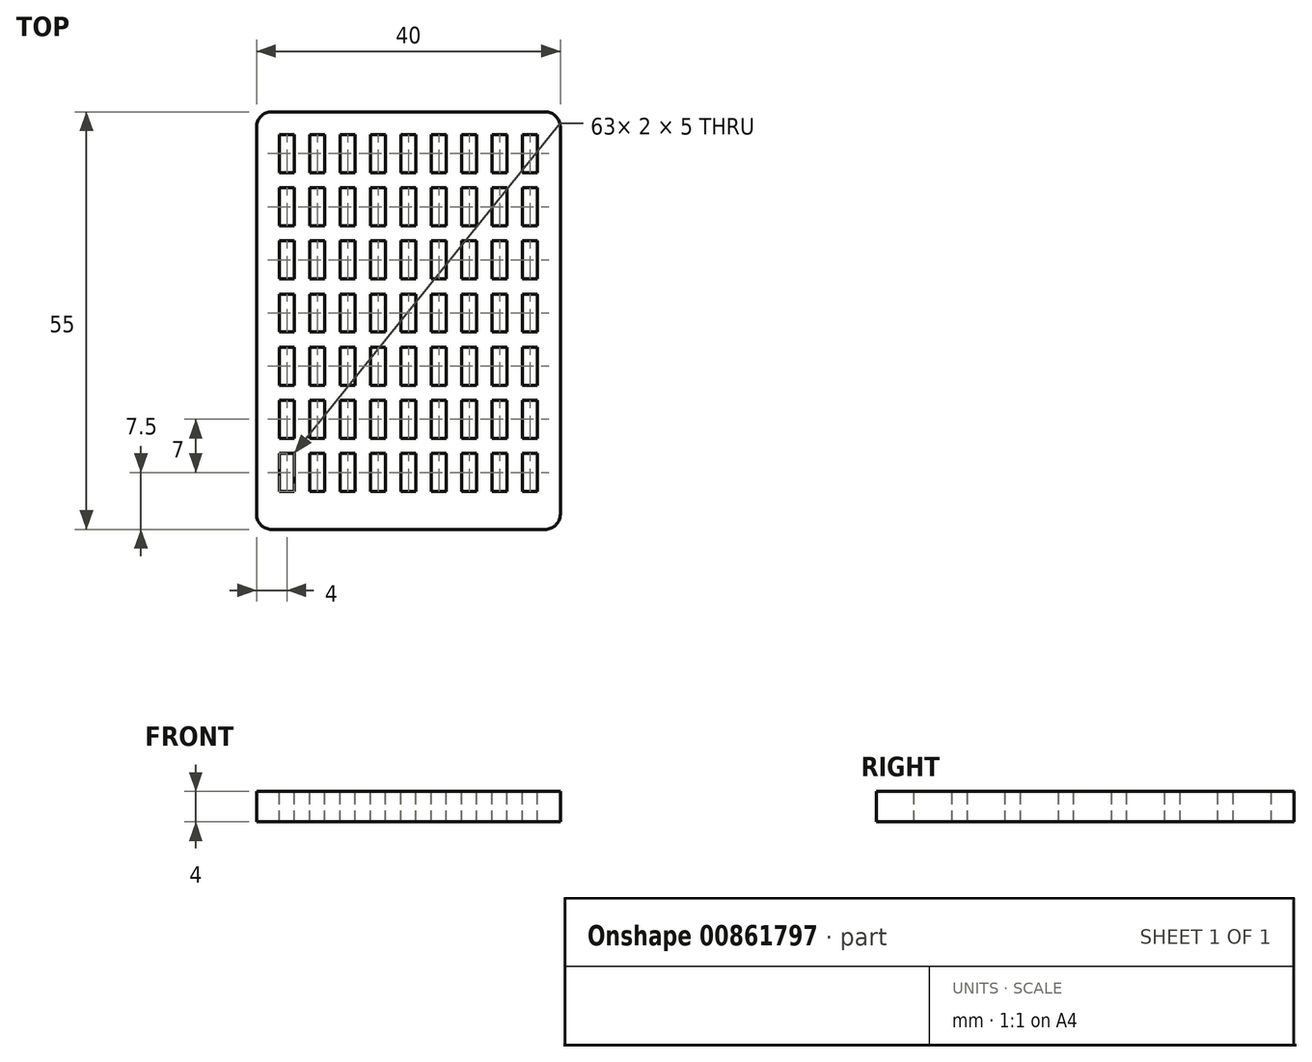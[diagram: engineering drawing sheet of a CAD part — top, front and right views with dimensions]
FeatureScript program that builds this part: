
annotation { "Feature Type Name" : "Feature", "Feature Type Description" : "" }
export const myFeature = defineFeature(function(context is Context, id is Id, definition is map)
    precondition{}
    {
        {
            var Q0;
            Q0=qCreatedBy(makeId("Top.planeOp"),FACE);
            var sketch = newSketch(context, id + "F0", { "sketchPlane" : qUnion([Q0])});
            skLineSegment(sketch, "E0.bottom", {"start": v(-20, 27.5) * mm, "end": v(20, 27.5) * mm});
            skLineSegment(sketch, "E0.top", {"start": v(-20, -27.5) * mm, "end": v(20, -27.5) * mm});
            skLineSegment(sketch, "E0.left", {"start": v(-20, 27.5) * mm, "end": v(-20, -27.5) * mm});
            skLineSegment(sketch, "E0.right", {"start": v(20, 27.5) * mm, "end": v(20, -27.5) * mm});
            skPoint(sketch, "E0.middle", {"position": v(0, 0) * mm});
            skSolve(sketch);
        }
        {
            var Q0;
            Q0 = qSketchRegion(id + "F0", true);
            extrude(context, id + "F1", {"entities" : qUnion([Q0]), "depth" : 4 * mm, "offsetDistance" : 25 * mm});
        }
        {
            var Q0;
            Q0=makeQuery(id+"F1.opExtrude","SWEPT_EDGE",EDGE,{"disambiguationData":[OSD([sQuery(id+"F0.wireOp",EDGE,"E0.bottom"),sQuery(id+"F0.wireOp",EDGE,"E0.left")])]});
            var Q1;
            Q1=makeQuery(id+"F1.opExtrude","SWEPT_EDGE",EDGE,{"disambiguationData":[OSD([sQuery(id+"F0.wireOp",EDGE,"E0.bottom"),sQuery(id+"F0.wireOp",EDGE,"E0.right")])]});
            var Q2;
            Q2=makeQuery(id+"F1.opExtrude","SWEPT_EDGE",EDGE,{"disambiguationData":[OSD([sQuery(id+"F0.wireOp",EDGE,"E0.top"),sQuery(id+"F0.wireOp",EDGE,"E0.left")])]});
            var Q3;
            Q3=makeQuery(id+"F1.opExtrude","SWEPT_EDGE",EDGE,{"disambiguationData":[OSD([sQuery(id+"F0.wireOp",EDGE,"E0.top"),sQuery(id+"F0.wireOp",EDGE,"E0.right")])]});
            fillet(context, id + "F2", {"entities" : qUnion([Q0, Q1, Q2, Q3]), "radius" : 2 * mm, "tangentPropagation" : true, "allowEdgeOverflow" : false});
        }
        {
            var Q0;
            Q0=makeQuery(id+"F1.opExtrude","CAP_FACE",FACE,{"disambiguationData":[OSD([sQuery(id+"F0.wireOp",EDGE,"E0.bottom"),sQuery(id+"F0.wireOp",EDGE,"E0.top"),sQuery(id+"F0.wireOp",EDGE,"E0.left"),sQuery(id+"F0.wireOp",EDGE,"E0.right")])],"isStart":false});
            var sketch = newSketch(context, id + "F3", { "sketchPlane" : qUnion([Q0])});
            skLineSegment(sketch, "E1.bottom", {"start": v(-17, 27.5) * mm, "end": v(-15, 27.5) * mm});
            skLineSegment(sketch, "E1.top", {"start": v(-17, -27.5) * mm, "end": v(-15, -27.5) * mm});
            skLineSegment(sketch, "E1.left", {"start": v(-17, 27.5) * mm, "end": v(-17, -27.5) * mm});
            skLineSegment(sketch, "E1.right", {"start": v(-15, 27.5) * mm, "end": v(-15, -27.5) * mm});
            skLineSegment(sketch, "E2.bottom", {"start": v(-13, -27.5) * mm, "end": v(-11, -27.5) * mm});
            skLineSegment(sketch, "E2.top", {"start": v(-13, 27.5) * mm, "end": v(-11, 27.5) * mm});
            skLineSegment(sketch, "E2.left", {"start": v(-13, -27.5) * mm, "end": v(-13, 27.5) * mm});
            skLineSegment(sketch, "E2.right", {"start": v(-11, -27.5) * mm, "end": v(-11, 27.5) * mm});
            skLineSegment(sketch, "E3.bottom", {"start": v(-9, 27.5) * mm, "end": v(-7, 27.5) * mm});
            skLineSegment(sketch, "E3.top", {"start": v(-9, -27.5) * mm, "end": v(-7, -27.5) * mm});
            skLineSegment(sketch, "E3.left", {"start": v(-9, 27.5) * mm, "end": v(-9, -27.5) * mm});
            skLineSegment(sketch, "E3.right", {"start": v(-7, 27.5) * mm, "end": v(-7, -27.5) * mm});
            skLineSegment(sketch, "E4.bottom", {"start": v(-5, -27.5) * mm, "end": v(-3, -27.5) * mm});
            skLineSegment(sketch, "E4.top", {"start": v(-5, 27.5) * mm, "end": v(-3, 27.5) * mm});
            skLineSegment(sketch, "E4.left", {"start": v(-5, -27.5) * mm, "end": v(-5, 27.5) * mm});
            skLineSegment(sketch, "E4.right", {"start": v(-3, -27.5) * mm, "end": v(-3, 27.5) * mm});
            skLineSegment(sketch, "E5.bottom", {"start": v(-1, 27.5) * mm, "end": v(1, 27.5) * mm});
            skLineSegment(sketch, "E5.top", {"start": v(-1, -27.5) * mm, "end": v(1, -27.5) * mm});
            skLineSegment(sketch, "E5.left", {"start": v(-1, 27.5) * mm, "end": v(-1, -27.5) * mm});
            skLineSegment(sketch, "E5.right", {"start": v(1, 27.5) * mm, "end": v(1, -27.5) * mm});
            skLineSegment(sketch, "E6.bottom", {"start": v(3, 27.5) * mm, "end": v(5, 27.5) * mm});
            skLineSegment(sketch, "E6.top", {"start": v(3, -27.5) * mm, "end": v(5, -27.5) * mm});
            skLineSegment(sketch, "E6.left", {"start": v(3, 27.5) * mm, "end": v(3, -27.5) * mm});
            skLineSegment(sketch, "E6.right", {"start": v(5, 27.5) * mm, "end": v(5, -27.5) * mm});
            skLineSegment(sketch, "E7.bottom", {"start": v(7, -27.5) * mm, "end": v(9, -27.5) * mm});
            skLineSegment(sketch, "E7.top", {"start": v(7, 27.5) * mm, "end": v(9, 27.5) * mm});
            skLineSegment(sketch, "E7.left", {"start": v(7, -27.5) * mm, "end": v(7, 27.5) * mm});
            skLineSegment(sketch, "E7.right", {"start": v(9, -27.5) * mm, "end": v(9, 27.5) * mm});
            skLineSegment(sketch, "E8.bottom", {"start": v(11, 27.5) * mm, "end": v(13, 27.5) * mm});
            skLineSegment(sketch, "E8.top", {"start": v(11, -27.5) * mm, "end": v(13, -27.5) * mm});
            skLineSegment(sketch, "E8.left", {"start": v(11, 27.5) * mm, "end": v(11, -27.5) * mm});
            skLineSegment(sketch, "E8.right", {"start": v(13, 27.5) * mm, "end": v(13, -27.5) * mm});
            skLineSegment(sketch, "E9.bottom", {"start": v(15, -27.5) * mm, "end": v(17, -27.5) * mm});
            skLineSegment(sketch, "E9.top", {"start": v(15, 27.5) * mm, "end": v(17, 27.5) * mm});
            skLineSegment(sketch, "E9.left", {"start": v(15, -27.5) * mm, "end": v(15, 27.5) * mm});
            skLineSegment(sketch, "E9.right", {"start": v(17, -27.5) * mm, "end": v(17, 27.5) * mm});
            skLineSegment(sketch, "E10.bottom", {"start": v(-20, 24.5) * mm, "end": v(20, 24.5) * mm});
            skLineSegment(sketch, "E10.top", {"start": v(-20, 19.5) * mm, "end": v(20, 19.5) * mm});
            skLineSegment(sketch, "E10.left", {"start": v(-20, 24.5) * mm, "end": v(-20, 19.5) * mm});
            skLineSegment(sketch, "E10.right", {"start": v(20, 24.5) * mm, "end": v(20, 19.5) * mm});
            skLineSegment(sketch, "E11.bottom", {"start": v(-20, 17.5) * mm, "end": v(20, 17.5) * mm});
            skLineSegment(sketch, "E11.top", {"start": v(-20, 12.5) * mm, "end": v(20, 12.5) * mm});
            skLineSegment(sketch, "E11.left", {"start": v(-20, 17.5) * mm, "end": v(-20, 12.5) * mm});
            skLineSegment(sketch, "E11.right", {"start": v(20, 17.5) * mm, "end": v(20, 12.5) * mm});
            skLineSegment(sketch, "E12.bottom", {"start": v(-20, 10.5) * mm, "end": v(20, 10.5) * mm});
            skLineSegment(sketch, "E12.top", {"start": v(-20, 5.5) * mm, "end": v(20, 5.5) * mm});
            skLineSegment(sketch, "E12.left", {"start": v(-20, 10.5) * mm, "end": v(-20, 5.5) * mm});
            skLineSegment(sketch, "E12.right", {"start": v(20, 10.5) * mm, "end": v(20, 5.5) * mm});
            skLineSegment(sketch, "E13.bottom", {"start": v(-20, 3.5) * mm, "end": v(20, 3.5) * mm});
            skLineSegment(sketch, "E13.top", {"start": v(-20, -1.5) * mm, "end": v(20, -1.5) * mm});
            skLineSegment(sketch, "E13.left", {"start": v(-20, 3.5) * mm, "end": v(-20, -1.5) * mm});
            skLineSegment(sketch, "E13.right", {"start": v(20, 3.5) * mm, "end": v(20, -1.5) * mm});
            skLineSegment(sketch, "E14.bottom", {"start": v(-20, -3.5) * mm, "end": v(20, -3.5) * mm});
            skLineSegment(sketch, "E14.top", {"start": v(-20, -8.5) * mm, "end": v(20, -8.5) * mm});
            skLineSegment(sketch, "E14.left", {"start": v(-20, -3.5) * mm, "end": v(-20, -8.5) * mm});
            skLineSegment(sketch, "E14.right", {"start": v(20, -3.5) * mm, "end": v(20, -8.5) * mm});
            skLineSegment(sketch, "E15.bottom", {"start": v(20, -8.5) * mm, "end": v(-20, -8.5) * mm});
            skLineSegment(sketch, "E15.top", {"start": v(20, -10.5) * mm, "end": v(-20, -10.5) * mm});
            skLineSegment(sketch, "E15.left", {"start": v(20, -8.5) * mm, "end": v(20, -10.5) * mm});
            skLineSegment(sketch, "E15.right", {"start": v(-20, -8.5) * mm, "end": v(-20, -10.5) * mm});
            skLineSegment(sketch, "E16.bottom", {"start": v(-20, -15.5) * mm, "end": v(20, -15.5) * mm});
            skLineSegment(sketch, "E16.top", {"start": v(-20, -17.5) * mm, "end": v(20, -17.5) * mm});
            skLineSegment(sketch, "E16.left", {"start": v(-20, -15.5) * mm, "end": v(-20, -17.5) * mm});
            skLineSegment(sketch, "E16.right", {"start": v(20, -15.5) * mm, "end": v(20, -17.5) * mm});
            skLineSegment(sketch, "E17.bottom", {"start": v(20, -22.5) * mm, "end": v(-20, -22.5) * mm});
            skLineSegment(sketch, "E17.top", {"start": v(20, -24.5) * mm, "end": v(-20, -24.5) * mm});
            skLineSegment(sketch, "E17.left", {"start": v(20, -22.5) * mm, "end": v(20, -24.5) * mm});
            skLineSegment(sketch, "E17.right", {"start": v(-20, -22.5) * mm, "end": v(-20, -24.5) * mm});
            skSolve(sketch);
        }
        {
            var Q0;
            {var subQ0=sQuery(id+"F3.wireOp",EDGE,"E10.bottom");var subQ1=sQuery(id+"F3.wireOp",EDGE,"E1.left");var subQ2=makeQuery(id+"F3.imprint","INTERSECT",VERTEX,{"derivedFrom":[subQ1,subQ0]});Q0=makeQuery(id+"F3.imprint","IMPRINT",FACE,{"disambiguationData":[TD([[makeQuery(id+"F3.imprint","IMPRINT",EDGE,{"disambiguationData":[TD([[subQ2,-1.0]])],"derivedFrom":subQ1}),1.0]])]});}
            var Q1;
            {var subQ0=sQuery(id+"F3.wireOp",EDGE,"E11.bottom");var subQ1=sQuery(id+"F3.wireOp",EDGE,"E1.left");var subQ2=makeQuery(id+"F3.imprint","INTERSECT",VERTEX,{"derivedFrom":[subQ1,subQ0]});Q1=makeQuery(id+"F3.imprint","IMPRINT",FACE,{"disambiguationData":[TD([[makeQuery(id+"F3.imprint","IMPRINT",EDGE,{"disambiguationData":[TD([[subQ2,-1.0]])],"derivedFrom":subQ1}),1.0]])]});}
            var Q2;
            {var subQ0=sQuery(id+"F3.wireOp",EDGE,"E12.bottom");var subQ1=sQuery(id+"F3.wireOp",EDGE,"E1.left");var subQ2=makeQuery(id+"F3.imprint","INTERSECT",VERTEX,{"derivedFrom":[subQ1,subQ0]});Q2=makeQuery(id+"F3.imprint","IMPRINT",FACE,{"disambiguationData":[TD([[makeQuery(id+"F3.imprint","IMPRINT",EDGE,{"disambiguationData":[TD([[subQ2,-1.0]])],"derivedFrom":subQ1}),1.0]])]});}
            var Q3;
            {var subQ0=sQuery(id+"F3.wireOp",EDGE,"E13.bottom");var subQ1=sQuery(id+"F3.wireOp",EDGE,"E1.left");var subQ2=makeQuery(id+"F3.imprint","INTERSECT",VERTEX,{"derivedFrom":[subQ1,subQ0]});Q3=makeQuery(id+"F3.imprint","IMPRINT",FACE,{"disambiguationData":[TD([[makeQuery(id+"F3.imprint","IMPRINT",EDGE,{"disambiguationData":[TD([[subQ2,-1.0]])],"derivedFrom":subQ1}),1.0]])]});}
            var Q4;
            {var subQ0=sQuery(id+"F3.wireOp",EDGE,"E14.bottom");var subQ1=sQuery(id+"F3.wireOp",EDGE,"E1.left");var subQ2=makeQuery(id+"F3.imprint","INTERSECT",VERTEX,{"derivedFrom":[subQ1,subQ0]});Q4=makeQuery(id+"F3.imprint","IMPRINT",FACE,{"disambiguationData":[TD([[makeQuery(id+"F3.imprint","IMPRINT",EDGE,{"disambiguationData":[TD([[subQ2,-1.0]])],"derivedFrom":subQ1}),1.0]])]});}
            var Q5;
            {var subQ0=sQuery(id+"F3.wireOp",EDGE,"E15.top");var subQ1=sQuery(id+"F3.wireOp",EDGE,"E1.left");var subQ2=makeQuery(id+"F3.imprint","INTERSECT",VERTEX,{"derivedFrom":[subQ1,subQ0]});Q5=makeQuery(id+"F3.imprint","IMPRINT",FACE,{"disambiguationData":[TD([[makeQuery(id+"F3.imprint","IMPRINT",EDGE,{"disambiguationData":[TD([[subQ2,-1.0]])],"derivedFrom":subQ1}),1.0]])]});}
            var Q6;
            {var subQ0=sQuery(id+"F3.wireOp",EDGE,"E17.bottom");var subQ1=sQuery(id+"F3.wireOp",EDGE,"E2.left");var subQ2=makeQuery(id+"F3.imprint","INTERSECT",VERTEX,{"derivedFrom":[subQ1,subQ0]});Q6=makeQuery(id+"F3.imprint","IMPRINT",FACE,{"disambiguationData":[TD([[makeQuery(id+"F3.imprint","IMPRINT",EDGE,{"disambiguationData":[TD([[subQ2,-1.0]])],"derivedFrom":subQ1}),-1.0]])]});}
            var Q7;
            {var subQ0=sQuery(id+"F3.wireOp",EDGE,"E16.bottom");var subQ1=sQuery(id+"F3.wireOp",EDGE,"E2.left");var subQ2=makeQuery(id+"F3.imprint","INTERSECT",VERTEX,{"derivedFrom":[subQ1,subQ0]});Q7=makeQuery(id+"F3.imprint","IMPRINT",FACE,{"disambiguationData":[TD([[makeQuery(id+"F3.imprint","IMPRINT",EDGE,{"disambiguationData":[TD([[subQ2,-1.0]])],"derivedFrom":subQ1}),-1.0]])]});}
            var Q8;
            {var subQ0=sQuery(id+"F3.wireOp",EDGE,"E15.bottom");var subQ1=sQuery(id+"F3.wireOp",EDGE,"E2.left");var subQ2=makeQuery(id+"F3.imprint","INTERSECT",VERTEX,{"derivedFrom":[subQ1,subQ0]});Q8=makeQuery(id+"F3.imprint","IMPRINT",FACE,{"disambiguationData":[TD([[makeQuery(id+"F3.imprint","IMPRINT",EDGE,{"disambiguationData":[TD([[subQ2,-1.0]])],"derivedFrom":subQ1}),-1.0]])]});}
            var Q9;
            {var subQ0=sQuery(id+"F3.wireOp",EDGE,"E13.top");var subQ1=sQuery(id+"F3.wireOp",EDGE,"E2.left");var subQ2=makeQuery(id+"F3.imprint","INTERSECT",VERTEX,{"derivedFrom":[subQ1,subQ0]});Q9=makeQuery(id+"F3.imprint","IMPRINT",FACE,{"disambiguationData":[TD([[makeQuery(id+"F3.imprint","IMPRINT",EDGE,{"disambiguationData":[TD([[subQ2,-1.0]])],"derivedFrom":subQ1}),-1.0]])]});}
            var Q10;
            {var subQ0=sQuery(id+"F3.wireOp",EDGE,"E12.top");var subQ1=sQuery(id+"F3.wireOp",EDGE,"E2.left");var subQ2=makeQuery(id+"F3.imprint","INTERSECT",VERTEX,{"derivedFrom":[subQ1,subQ0]});Q10=makeQuery(id+"F3.imprint","IMPRINT",FACE,{"disambiguationData":[TD([[makeQuery(id+"F3.imprint","IMPRINT",EDGE,{"disambiguationData":[TD([[subQ2,-1.0]])],"derivedFrom":subQ1}),-1.0]])]});}
            var Q11;
            {var subQ0=sQuery(id+"F3.wireOp",EDGE,"E11.top");var subQ1=sQuery(id+"F3.wireOp",EDGE,"E2.left");var subQ2=makeQuery(id+"F3.imprint","INTERSECT",VERTEX,{"derivedFrom":[subQ1,subQ0]});Q11=makeQuery(id+"F3.imprint","IMPRINT",FACE,{"disambiguationData":[TD([[makeQuery(id+"F3.imprint","IMPRINT",EDGE,{"disambiguationData":[TD([[subQ2,-1.0]])],"derivedFrom":subQ1}),-1.0]])]});}
            var Q12;
            {var subQ0=sQuery(id+"F3.wireOp",EDGE,"E10.top");var subQ1=sQuery(id+"F3.wireOp",EDGE,"E2.left");var subQ2=makeQuery(id+"F3.imprint","INTERSECT",VERTEX,{"derivedFrom":[subQ1,subQ0]});Q12=makeQuery(id+"F3.imprint","IMPRINT",FACE,{"disambiguationData":[TD([[makeQuery(id+"F3.imprint","IMPRINT",EDGE,{"disambiguationData":[TD([[subQ2,-1.0]])],"derivedFrom":subQ1}),-1.0]])]});}
            var Q13;
            {var subQ0=sQuery(id+"F3.wireOp",EDGE,"E10.bottom");var subQ1=sQuery(id+"F3.wireOp",EDGE,"E3.left");var subQ2=makeQuery(id+"F3.imprint","INTERSECT",VERTEX,{"derivedFrom":[subQ1,subQ0]});Q13=makeQuery(id+"F3.imprint","IMPRINT",FACE,{"disambiguationData":[TD([[makeQuery(id+"F3.imprint","IMPRINT",EDGE,{"disambiguationData":[TD([[subQ2,-1.0]])],"derivedFrom":subQ1}),1.0]])]});}
            var Q14;
            {var subQ0=sQuery(id+"F3.wireOp",EDGE,"E11.bottom");var subQ1=sQuery(id+"F3.wireOp",EDGE,"E3.left");var subQ2=makeQuery(id+"F3.imprint","INTERSECT",VERTEX,{"derivedFrom":[subQ1,subQ0]});Q14=makeQuery(id+"F3.imprint","IMPRINT",FACE,{"disambiguationData":[TD([[makeQuery(id+"F3.imprint","IMPRINT",EDGE,{"disambiguationData":[TD([[subQ2,-1.0]])],"derivedFrom":subQ1}),1.0]])]});}
            var Q15;
            {var subQ0=sQuery(id+"F3.wireOp",EDGE,"E12.bottom");var subQ1=sQuery(id+"F3.wireOp",EDGE,"E3.left");var subQ2=makeQuery(id+"F3.imprint","INTERSECT",VERTEX,{"derivedFrom":[subQ1,subQ0]});Q15=makeQuery(id+"F3.imprint","IMPRINT",FACE,{"disambiguationData":[TD([[makeQuery(id+"F3.imprint","IMPRINT",EDGE,{"disambiguationData":[TD([[subQ2,-1.0]])],"derivedFrom":subQ1}),1.0]])]});}
            var Q16;
            {var subQ0=sQuery(id+"F3.wireOp",EDGE,"E13.bottom");var subQ1=sQuery(id+"F3.wireOp",EDGE,"E3.left");var subQ2=makeQuery(id+"F3.imprint","INTERSECT",VERTEX,{"derivedFrom":[subQ1,subQ0]});Q16=makeQuery(id+"F3.imprint","IMPRINT",FACE,{"disambiguationData":[TD([[makeQuery(id+"F3.imprint","IMPRINT",EDGE,{"disambiguationData":[TD([[subQ2,-1.0]])],"derivedFrom":subQ1}),1.0]])]});}
            var Q17;
            {var subQ0=sQuery(id+"F3.wireOp",EDGE,"E14.bottom");var subQ1=sQuery(id+"F3.wireOp",EDGE,"E3.left");var subQ2=makeQuery(id+"F3.imprint","INTERSECT",VERTEX,{"derivedFrom":[subQ1,subQ0]});Q17=makeQuery(id+"F3.imprint","IMPRINT",FACE,{"disambiguationData":[TD([[makeQuery(id+"F3.imprint","IMPRINT",EDGE,{"disambiguationData":[TD([[subQ2,-1.0]])],"derivedFrom":subQ1}),1.0]])]});}
            var Q18;
            {var subQ0=sQuery(id+"F3.wireOp",EDGE,"E15.top");var subQ1=sQuery(id+"F3.wireOp",EDGE,"E3.left");var subQ2=makeQuery(id+"F3.imprint","INTERSECT",VERTEX,{"derivedFrom":[subQ1,subQ0]});Q18=makeQuery(id+"F3.imprint","IMPRINT",FACE,{"disambiguationData":[TD([[makeQuery(id+"F3.imprint","IMPRINT",EDGE,{"disambiguationData":[TD([[subQ2,-1.0]])],"derivedFrom":subQ1}),1.0]])]});}
            var Q19;
            {var subQ0=sQuery(id+"F3.wireOp",EDGE,"E16.top");var subQ1=sQuery(id+"F3.wireOp",EDGE,"E1.left");var subQ2=makeQuery(id+"F3.imprint","INTERSECT",VERTEX,{"derivedFrom":[subQ1,subQ0]});Q19=makeQuery(id+"F3.imprint","IMPRINT",FACE,{"disambiguationData":[TD([[makeQuery(id+"F3.imprint","IMPRINT",EDGE,{"disambiguationData":[TD([[subQ2,-1.0]])],"derivedFrom":subQ1}),1.0]])]});}
            var Q20;
            {var subQ0=sQuery(id+"F3.wireOp",EDGE,"E16.top");var subQ1=sQuery(id+"F3.wireOp",EDGE,"E3.left");var subQ2=makeQuery(id+"F3.imprint","INTERSECT",VERTEX,{"derivedFrom":[subQ1,subQ0]});Q20=makeQuery(id+"F3.imprint","IMPRINT",FACE,{"disambiguationData":[TD([[makeQuery(id+"F3.imprint","IMPRINT",EDGE,{"disambiguationData":[TD([[subQ2,-1.0]])],"derivedFrom":subQ1}),1.0]])]});}
            var Q21;
            {var subQ0=sQuery(id+"F3.wireOp",EDGE,"E17.bottom");var subQ1=sQuery(id+"F3.wireOp",EDGE,"E4.left");var subQ2=makeQuery(id+"F3.imprint","INTERSECT",VERTEX,{"derivedFrom":[subQ1,subQ0]});Q21=makeQuery(id+"F3.imprint","IMPRINT",FACE,{"disambiguationData":[TD([[makeQuery(id+"F3.imprint","IMPRINT",EDGE,{"disambiguationData":[TD([[subQ2,-1.0]])],"derivedFrom":subQ1}),-1.0]])]});}
            var Q22;
            {var subQ0=sQuery(id+"F3.wireOp",EDGE,"E16.bottom");var subQ1=sQuery(id+"F3.wireOp",EDGE,"E4.left");var subQ2=makeQuery(id+"F3.imprint","INTERSECT",VERTEX,{"derivedFrom":[subQ1,subQ0]});Q22=makeQuery(id+"F3.imprint","IMPRINT",FACE,{"disambiguationData":[TD([[makeQuery(id+"F3.imprint","IMPRINT",EDGE,{"disambiguationData":[TD([[subQ2,-1.0]])],"derivedFrom":subQ1}),-1.0]])]});}
            var Q23;
            {var subQ0=sQuery(id+"F3.wireOp",EDGE,"E15.bottom");var subQ1=sQuery(id+"F3.wireOp",EDGE,"E4.left");var subQ2=makeQuery(id+"F3.imprint","INTERSECT",VERTEX,{"derivedFrom":[subQ1,subQ0]});Q23=makeQuery(id+"F3.imprint","IMPRINT",FACE,{"disambiguationData":[TD([[makeQuery(id+"F3.imprint","IMPRINT",EDGE,{"disambiguationData":[TD([[subQ2,-1.0]])],"derivedFrom":subQ1}),-1.0]])]});}
            var Q24;
            {var subQ0=sQuery(id+"F3.wireOp",EDGE,"E13.top");var subQ1=sQuery(id+"F3.wireOp",EDGE,"E4.left");var subQ2=makeQuery(id+"F3.imprint","INTERSECT",VERTEX,{"derivedFrom":[subQ1,subQ0]});Q24=makeQuery(id+"F3.imprint","IMPRINT",FACE,{"disambiguationData":[TD([[makeQuery(id+"F3.imprint","IMPRINT",EDGE,{"disambiguationData":[TD([[subQ2,-1.0]])],"derivedFrom":subQ1}),-1.0]])]});}
            var Q25;
            {var subQ0=sQuery(id+"F3.wireOp",EDGE,"E12.top");var subQ1=sQuery(id+"F3.wireOp",EDGE,"E4.left");var subQ2=makeQuery(id+"F3.imprint","INTERSECT",VERTEX,{"derivedFrom":[subQ1,subQ0]});Q25=makeQuery(id+"F3.imprint","IMPRINT",FACE,{"disambiguationData":[TD([[makeQuery(id+"F3.imprint","IMPRINT",EDGE,{"disambiguationData":[TD([[subQ2,-1.0]])],"derivedFrom":subQ1}),-1.0]])]});}
            var Q26;
            {var subQ0=sQuery(id+"F3.wireOp",EDGE,"E11.top");var subQ1=sQuery(id+"F3.wireOp",EDGE,"E4.left");var subQ2=makeQuery(id+"F3.imprint","INTERSECT",VERTEX,{"derivedFrom":[subQ1,subQ0]});Q26=makeQuery(id+"F3.imprint","IMPRINT",FACE,{"disambiguationData":[TD([[makeQuery(id+"F3.imprint","IMPRINT",EDGE,{"disambiguationData":[TD([[subQ2,-1.0]])],"derivedFrom":subQ1}),-1.0]])]});}
            var Q27;
            {var subQ0=sQuery(id+"F3.wireOp",EDGE,"E10.top");var subQ1=sQuery(id+"F3.wireOp",EDGE,"E4.left");var subQ2=makeQuery(id+"F3.imprint","INTERSECT",VERTEX,{"derivedFrom":[subQ1,subQ0]});Q27=makeQuery(id+"F3.imprint","IMPRINT",FACE,{"disambiguationData":[TD([[makeQuery(id+"F3.imprint","IMPRINT",EDGE,{"disambiguationData":[TD([[subQ2,-1.0]])],"derivedFrom":subQ1}),-1.0]])]});}
            var Q28;
            {var subQ0=sQuery(id+"F3.wireOp",EDGE,"E10.bottom");var subQ1=sQuery(id+"F3.wireOp",EDGE,"E5.left");var subQ2=makeQuery(id+"F3.imprint","INTERSECT",VERTEX,{"derivedFrom":[subQ1,subQ0]});Q28=makeQuery(id+"F3.imprint","IMPRINT",FACE,{"disambiguationData":[TD([[makeQuery(id+"F3.imprint","IMPRINT",EDGE,{"disambiguationData":[TD([[subQ2,-1.0]])],"derivedFrom":subQ1}),1.0]])]});}
            var Q29;
            {var subQ0=sQuery(id+"F3.wireOp",EDGE,"E11.bottom");var subQ1=sQuery(id+"F3.wireOp",EDGE,"E5.left");var subQ2=makeQuery(id+"F3.imprint","INTERSECT",VERTEX,{"derivedFrom":[subQ1,subQ0]});Q29=makeQuery(id+"F3.imprint","IMPRINT",FACE,{"disambiguationData":[TD([[makeQuery(id+"F3.imprint","IMPRINT",EDGE,{"disambiguationData":[TD([[subQ2,-1.0]])],"derivedFrom":subQ1}),1.0]])]});}
            var Q30;
            {var subQ0=sQuery(id+"F3.wireOp",EDGE,"E12.bottom");var subQ1=sQuery(id+"F3.wireOp",EDGE,"E5.left");var subQ2=makeQuery(id+"F3.imprint","INTERSECT",VERTEX,{"derivedFrom":[subQ1,subQ0]});Q30=makeQuery(id+"F3.imprint","IMPRINT",FACE,{"disambiguationData":[TD([[makeQuery(id+"F3.imprint","IMPRINT",EDGE,{"disambiguationData":[TD([[subQ2,-1.0]])],"derivedFrom":subQ1}),1.0]])]});}
            var Q31;
            {var subQ0=sQuery(id+"F3.wireOp",EDGE,"E13.bottom");var subQ1=sQuery(id+"F3.wireOp",EDGE,"E5.left");var subQ2=makeQuery(id+"F3.imprint","INTERSECT",VERTEX,{"derivedFrom":[subQ1,subQ0]});Q31=makeQuery(id+"F3.imprint","IMPRINT",FACE,{"disambiguationData":[TD([[makeQuery(id+"F3.imprint","IMPRINT",EDGE,{"disambiguationData":[TD([[subQ2,-1.0]])],"derivedFrom":subQ1}),1.0]])]});}
            var Q32;
            {var subQ0=sQuery(id+"F3.wireOp",EDGE,"E14.bottom");var subQ1=sQuery(id+"F3.wireOp",EDGE,"E5.left");var subQ2=makeQuery(id+"F3.imprint","INTERSECT",VERTEX,{"derivedFrom":[subQ1,subQ0]});Q32=makeQuery(id+"F3.imprint","IMPRINT",FACE,{"disambiguationData":[TD([[makeQuery(id+"F3.imprint","IMPRINT",EDGE,{"disambiguationData":[TD([[subQ2,-1.0]])],"derivedFrom":subQ1}),1.0]])]});}
            var Q33;
            {var subQ0=sQuery(id+"F3.wireOp",EDGE,"E15.top");var subQ1=sQuery(id+"F3.wireOp",EDGE,"E5.left");var subQ2=makeQuery(id+"F3.imprint","INTERSECT",VERTEX,{"derivedFrom":[subQ1,subQ0]});Q33=makeQuery(id+"F3.imprint","IMPRINT",FACE,{"disambiguationData":[TD([[makeQuery(id+"F3.imprint","IMPRINT",EDGE,{"disambiguationData":[TD([[subQ2,-1.0]])],"derivedFrom":subQ1}),1.0]])]});}
            var Q34;
            {var subQ0=sQuery(id+"F3.wireOp",EDGE,"E16.top");var subQ1=sQuery(id+"F3.wireOp",EDGE,"E5.left");var subQ2=makeQuery(id+"F3.imprint","INTERSECT",VERTEX,{"derivedFrom":[subQ1,subQ0]});Q34=makeQuery(id+"F3.imprint","IMPRINT",FACE,{"disambiguationData":[TD([[makeQuery(id+"F3.imprint","IMPRINT",EDGE,{"disambiguationData":[TD([[subQ2,-1.0]])],"derivedFrom":subQ1}),1.0]])]});}
            var Q35;
            {var subQ0=sQuery(id+"F3.wireOp",EDGE,"E16.top");var subQ1=sQuery(id+"F3.wireOp",EDGE,"E6.left");var subQ2=makeQuery(id+"F3.imprint","INTERSECT",VERTEX,{"derivedFrom":[subQ1,subQ0]});Q35=makeQuery(id+"F3.imprint","IMPRINT",FACE,{"disambiguationData":[TD([[makeQuery(id+"F3.imprint","IMPRINT",EDGE,{"disambiguationData":[TD([[subQ2,-1.0]])],"derivedFrom":subQ1}),1.0]])]});}
            var Q36;
            {var subQ0=sQuery(id+"F3.wireOp",EDGE,"E15.top");var subQ1=sQuery(id+"F3.wireOp",EDGE,"E6.left");var subQ2=makeQuery(id+"F3.imprint","INTERSECT",VERTEX,{"derivedFrom":[subQ1,subQ0]});Q36=makeQuery(id+"F3.imprint","IMPRINT",FACE,{"disambiguationData":[TD([[makeQuery(id+"F3.imprint","IMPRINT",EDGE,{"disambiguationData":[TD([[subQ2,-1.0]])],"derivedFrom":subQ1}),1.0]])]});}
            var Q37;
            {var subQ0=sQuery(id+"F3.wireOp",EDGE,"E14.bottom");var subQ1=sQuery(id+"F3.wireOp",EDGE,"E6.left");var subQ2=makeQuery(id+"F3.imprint","INTERSECT",VERTEX,{"derivedFrom":[subQ1,subQ0]});Q37=makeQuery(id+"F3.imprint","IMPRINT",FACE,{"disambiguationData":[TD([[makeQuery(id+"F3.imprint","IMPRINT",EDGE,{"disambiguationData":[TD([[subQ2,-1.0]])],"derivedFrom":subQ1}),1.0]])]});}
            var Q38;
            {var subQ0=sQuery(id+"F3.wireOp",EDGE,"E13.bottom");var subQ1=sQuery(id+"F3.wireOp",EDGE,"E6.left");var subQ2=makeQuery(id+"F3.imprint","INTERSECT",VERTEX,{"derivedFrom":[subQ1,subQ0]});Q38=makeQuery(id+"F3.imprint","IMPRINT",FACE,{"disambiguationData":[TD([[makeQuery(id+"F3.imprint","IMPRINT",EDGE,{"disambiguationData":[TD([[subQ2,-1.0]])],"derivedFrom":subQ1}),1.0]])]});}
            var Q39;
            {var subQ0=sQuery(id+"F3.wireOp",EDGE,"E12.bottom");var subQ1=sQuery(id+"F3.wireOp",EDGE,"E6.left");var subQ2=makeQuery(id+"F3.imprint","INTERSECT",VERTEX,{"derivedFrom":[subQ1,subQ0]});Q39=makeQuery(id+"F3.imprint","IMPRINT",FACE,{"disambiguationData":[TD([[makeQuery(id+"F3.imprint","IMPRINT",EDGE,{"disambiguationData":[TD([[subQ2,-1.0]])],"derivedFrom":subQ1}),1.0]])]});}
            var Q40;
            {var subQ0=sQuery(id+"F3.wireOp",EDGE,"E11.bottom");var subQ1=sQuery(id+"F3.wireOp",EDGE,"E6.left");var subQ2=makeQuery(id+"F3.imprint","INTERSECT",VERTEX,{"derivedFrom":[subQ1,subQ0]});Q40=makeQuery(id+"F3.imprint","IMPRINT",FACE,{"disambiguationData":[TD([[makeQuery(id+"F3.imprint","IMPRINT",EDGE,{"disambiguationData":[TD([[subQ2,-1.0]])],"derivedFrom":subQ1}),1.0]])]});}
            var Q41;
            {var subQ0=sQuery(id+"F3.wireOp",EDGE,"E10.bottom");var subQ1=sQuery(id+"F3.wireOp",EDGE,"E6.left");var subQ2=makeQuery(id+"F3.imprint","INTERSECT",VERTEX,{"derivedFrom":[subQ1,subQ0]});Q41=makeQuery(id+"F3.imprint","IMPRINT",FACE,{"disambiguationData":[TD([[makeQuery(id+"F3.imprint","IMPRINT",EDGE,{"disambiguationData":[TD([[subQ2,-1.0]])],"derivedFrom":subQ1}),1.0]])]});}
            var Q42;
            {var subQ0=sQuery(id+"F3.wireOp",EDGE,"E10.top");var subQ1=sQuery(id+"F3.wireOp",EDGE,"E7.left");var subQ2=makeQuery(id+"F3.imprint","INTERSECT",VERTEX,{"derivedFrom":[subQ1,subQ0]});Q42=makeQuery(id+"F3.imprint","IMPRINT",FACE,{"disambiguationData":[TD([[makeQuery(id+"F3.imprint","IMPRINT",EDGE,{"disambiguationData":[TD([[subQ2,-1.0]])],"derivedFrom":subQ1}),-1.0]])]});}
            var Q43;
            {var subQ0=sQuery(id+"F3.wireOp",EDGE,"E11.top");var subQ1=sQuery(id+"F3.wireOp",EDGE,"E7.left");var subQ2=makeQuery(id+"F3.imprint","INTERSECT",VERTEX,{"derivedFrom":[subQ1,subQ0]});Q43=makeQuery(id+"F3.imprint","IMPRINT",FACE,{"disambiguationData":[TD([[makeQuery(id+"F3.imprint","IMPRINT",EDGE,{"disambiguationData":[TD([[subQ2,-1.0]])],"derivedFrom":subQ1}),-1.0]])]});}
            var Q44;
            {var subQ0=sQuery(id+"F3.wireOp",EDGE,"E12.top");var subQ1=sQuery(id+"F3.wireOp",EDGE,"E7.left");var subQ2=makeQuery(id+"F3.imprint","INTERSECT",VERTEX,{"derivedFrom":[subQ1,subQ0]});Q44=makeQuery(id+"F3.imprint","IMPRINT",FACE,{"disambiguationData":[TD([[makeQuery(id+"F3.imprint","IMPRINT",EDGE,{"disambiguationData":[TD([[subQ2,-1.0]])],"derivedFrom":subQ1}),-1.0]])]});}
            var Q45;
            {var subQ0=sQuery(id+"F3.wireOp",EDGE,"E13.top");var subQ1=sQuery(id+"F3.wireOp",EDGE,"E7.left");var subQ2=makeQuery(id+"F3.imprint","INTERSECT",VERTEX,{"derivedFrom":[subQ1,subQ0]});Q45=makeQuery(id+"F3.imprint","IMPRINT",FACE,{"disambiguationData":[TD([[makeQuery(id+"F3.imprint","IMPRINT",EDGE,{"disambiguationData":[TD([[subQ2,-1.0]])],"derivedFrom":subQ1}),-1.0]])]});}
            var Q46;
            {var subQ0=sQuery(id+"F3.wireOp",EDGE,"E15.bottom");var subQ1=sQuery(id+"F3.wireOp",EDGE,"E7.left");var subQ2=makeQuery(id+"F3.imprint","INTERSECT",VERTEX,{"derivedFrom":[subQ1,subQ0]});Q46=makeQuery(id+"F3.imprint","IMPRINT",FACE,{"disambiguationData":[TD([[makeQuery(id+"F3.imprint","IMPRINT",EDGE,{"disambiguationData":[TD([[subQ2,-1.0]])],"derivedFrom":subQ1}),-1.0]])]});}
            var Q47;
            {var subQ0=sQuery(id+"F3.wireOp",EDGE,"E16.bottom");var subQ1=sQuery(id+"F3.wireOp",EDGE,"E7.left");var subQ2=makeQuery(id+"F3.imprint","INTERSECT",VERTEX,{"derivedFrom":[subQ1,subQ0]});Q47=makeQuery(id+"F3.imprint","IMPRINT",FACE,{"disambiguationData":[TD([[makeQuery(id+"F3.imprint","IMPRINT",EDGE,{"disambiguationData":[TD([[subQ2,-1.0]])],"derivedFrom":subQ1}),-1.0]])]});}
            var Q48;
            {var subQ0=sQuery(id+"F3.wireOp",EDGE,"E17.bottom");var subQ1=sQuery(id+"F3.wireOp",EDGE,"E7.left");var subQ2=makeQuery(id+"F3.imprint","INTERSECT",VERTEX,{"derivedFrom":[subQ1,subQ0]});Q48=makeQuery(id+"F3.imprint","IMPRINT",FACE,{"disambiguationData":[TD([[makeQuery(id+"F3.imprint","IMPRINT",EDGE,{"disambiguationData":[TD([[subQ2,-1.0]])],"derivedFrom":subQ1}),-1.0]])]});}
            var Q49;
            {var subQ0=sQuery(id+"F3.wireOp",EDGE,"E16.top");var subQ1=sQuery(id+"F3.wireOp",EDGE,"E8.left");var subQ2=makeQuery(id+"F3.imprint","INTERSECT",VERTEX,{"derivedFrom":[subQ1,subQ0]});Q49=makeQuery(id+"F3.imprint","IMPRINT",FACE,{"disambiguationData":[TD([[makeQuery(id+"F3.imprint","IMPRINT",EDGE,{"disambiguationData":[TD([[subQ2,-1.0]])],"derivedFrom":subQ1}),1.0]])]});}
            var Q50;
            {var subQ0=sQuery(id+"F3.wireOp",EDGE,"E15.top");var subQ1=sQuery(id+"F3.wireOp",EDGE,"E8.left");var subQ2=makeQuery(id+"F3.imprint","INTERSECT",VERTEX,{"derivedFrom":[subQ1,subQ0]});Q50=makeQuery(id+"F3.imprint","IMPRINT",FACE,{"disambiguationData":[TD([[makeQuery(id+"F3.imprint","IMPRINT",EDGE,{"disambiguationData":[TD([[subQ2,-1.0]])],"derivedFrom":subQ1}),1.0]])]});}
            var Q51;
            {var subQ0=sQuery(id+"F3.wireOp",EDGE,"E14.bottom");var subQ1=sQuery(id+"F3.wireOp",EDGE,"E8.left");var subQ2=makeQuery(id+"F3.imprint","INTERSECT",VERTEX,{"derivedFrom":[subQ1,subQ0]});Q51=makeQuery(id+"F3.imprint","IMPRINT",FACE,{"disambiguationData":[TD([[makeQuery(id+"F3.imprint","IMPRINT",EDGE,{"disambiguationData":[TD([[subQ2,-1.0]])],"derivedFrom":subQ1}),1.0]])]});}
            var Q52;
            {var subQ0=sQuery(id+"F3.wireOp",EDGE,"E13.bottom");var subQ1=sQuery(id+"F3.wireOp",EDGE,"E8.left");var subQ2=makeQuery(id+"F3.imprint","INTERSECT",VERTEX,{"derivedFrom":[subQ1,subQ0]});Q52=makeQuery(id+"F3.imprint","IMPRINT",FACE,{"disambiguationData":[TD([[makeQuery(id+"F3.imprint","IMPRINT",EDGE,{"disambiguationData":[TD([[subQ2,-1.0]])],"derivedFrom":subQ1}),1.0]])]});}
            var Q53;
            {var subQ0=sQuery(id+"F3.wireOp",EDGE,"E12.bottom");var subQ1=sQuery(id+"F3.wireOp",EDGE,"E8.left");var subQ2=makeQuery(id+"F3.imprint","INTERSECT",VERTEX,{"derivedFrom":[subQ1,subQ0]});Q53=makeQuery(id+"F3.imprint","IMPRINT",FACE,{"disambiguationData":[TD([[makeQuery(id+"F3.imprint","IMPRINT",EDGE,{"disambiguationData":[TD([[subQ2,-1.0]])],"derivedFrom":subQ1}),1.0]])]});}
            var Q54;
            {var subQ0=sQuery(id+"F3.wireOp",EDGE,"E11.bottom");var subQ1=sQuery(id+"F3.wireOp",EDGE,"E8.left");var subQ2=makeQuery(id+"F3.imprint","INTERSECT",VERTEX,{"derivedFrom":[subQ1,subQ0]});Q54=makeQuery(id+"F3.imprint","IMPRINT",FACE,{"disambiguationData":[TD([[makeQuery(id+"F3.imprint","IMPRINT",EDGE,{"disambiguationData":[TD([[subQ2,-1.0]])],"derivedFrom":subQ1}),1.0]])]});}
            var Q55;
            {var subQ0=sQuery(id+"F3.wireOp",EDGE,"E10.bottom");var subQ1=sQuery(id+"F3.wireOp",EDGE,"E8.left");var subQ2=makeQuery(id+"F3.imprint","INTERSECT",VERTEX,{"derivedFrom":[subQ1,subQ0]});Q55=makeQuery(id+"F3.imprint","IMPRINT",FACE,{"disambiguationData":[TD([[makeQuery(id+"F3.imprint","IMPRINT",EDGE,{"disambiguationData":[TD([[subQ2,-1.0]])],"derivedFrom":subQ1}),1.0]])]});}
            var Q56;
            {var subQ0=sQuery(id+"F3.wireOp",EDGE,"E10.top");var subQ1=sQuery(id+"F3.wireOp",EDGE,"E9.left");var subQ2=makeQuery(id+"F3.imprint","INTERSECT",VERTEX,{"derivedFrom":[subQ1,subQ0]});Q56=makeQuery(id+"F3.imprint","IMPRINT",FACE,{"disambiguationData":[TD([[makeQuery(id+"F3.imprint","IMPRINT",EDGE,{"disambiguationData":[TD([[subQ2,-1.0]])],"derivedFrom":subQ1}),-1.0]])]});}
            var Q57;
            {var subQ0=sQuery(id+"F3.wireOp",EDGE,"E11.top");var subQ1=sQuery(id+"F3.wireOp",EDGE,"E9.left");var subQ2=makeQuery(id+"F3.imprint","INTERSECT",VERTEX,{"derivedFrom":[subQ1,subQ0]});Q57=makeQuery(id+"F3.imprint","IMPRINT",FACE,{"disambiguationData":[TD([[makeQuery(id+"F3.imprint","IMPRINT",EDGE,{"disambiguationData":[TD([[subQ2,-1.0]])],"derivedFrom":subQ1}),-1.0]])]});}
            var Q58;
            {var subQ0=sQuery(id+"F3.wireOp",EDGE,"E12.top");var subQ1=sQuery(id+"F3.wireOp",EDGE,"E9.left");var subQ2=makeQuery(id+"F3.imprint","INTERSECT",VERTEX,{"derivedFrom":[subQ1,subQ0]});Q58=makeQuery(id+"F3.imprint","IMPRINT",FACE,{"disambiguationData":[TD([[makeQuery(id+"F3.imprint","IMPRINT",EDGE,{"disambiguationData":[TD([[subQ2,-1.0]])],"derivedFrom":subQ1}),-1.0]])]});}
            var Q59;
            {var subQ0=sQuery(id+"F3.wireOp",EDGE,"E13.top");var subQ1=sQuery(id+"F3.wireOp",EDGE,"E9.left");var subQ2=makeQuery(id+"F3.imprint","INTERSECT",VERTEX,{"derivedFrom":[subQ1,subQ0]});Q59=makeQuery(id+"F3.imprint","IMPRINT",FACE,{"disambiguationData":[TD([[makeQuery(id+"F3.imprint","IMPRINT",EDGE,{"disambiguationData":[TD([[subQ2,-1.0]])],"derivedFrom":subQ1}),-1.0]])]});}
            var Q60;
            {var subQ0=sQuery(id+"F3.wireOp",EDGE,"E15.bottom");var subQ1=sQuery(id+"F3.wireOp",EDGE,"E9.left");var subQ2=makeQuery(id+"F3.imprint","INTERSECT",VERTEX,{"derivedFrom":[subQ1,subQ0]});Q60=makeQuery(id+"F3.imprint","IMPRINT",FACE,{"disambiguationData":[TD([[makeQuery(id+"F3.imprint","IMPRINT",EDGE,{"disambiguationData":[TD([[subQ2,-1.0]])],"derivedFrom":subQ1}),-1.0]])]});}
            var Q61;
            {var subQ0=sQuery(id+"F3.wireOp",EDGE,"E16.bottom");var subQ1=sQuery(id+"F3.wireOp",EDGE,"E9.left");var subQ2=makeQuery(id+"F3.imprint","INTERSECT",VERTEX,{"derivedFrom":[subQ1,subQ0]});Q61=makeQuery(id+"F3.imprint","IMPRINT",FACE,{"disambiguationData":[TD([[makeQuery(id+"F3.imprint","IMPRINT",EDGE,{"disambiguationData":[TD([[subQ2,-1.0]])],"derivedFrom":subQ1}),-1.0]])]});}
            var Q62;
            {var subQ0=sQuery(id+"F3.wireOp",EDGE,"E17.bottom");var subQ1=sQuery(id+"F3.wireOp",EDGE,"E9.left");var subQ2=makeQuery(id+"F3.imprint","INTERSECT",VERTEX,{"derivedFrom":[subQ1,subQ0]});Q62=makeQuery(id+"F3.imprint","IMPRINT",FACE,{"disambiguationData":[TD([[makeQuery(id+"F3.imprint","IMPRINT",EDGE,{"disambiguationData":[TD([[subQ2,-1.0]])],"derivedFrom":subQ1}),-1.0]])]});}
            extrude(context, id + "F4", {"entities" : qUnion([Q0, Q1, Q2, Q3, Q4, Q5, Q6, Q7, Q8, Q9, Q10, Q11, Q12, Q13, Q14, Q15, Q16, Q17, Q18, Q19, Q20, Q21, Q22, Q23, Q24, Q25, Q26, Q27, Q28, Q29, Q30, Q31, Q32, Q33, Q34, Q35, Q36, Q37, Q38, Q39, Q40, Q41, Q42, Q43, Q44, Q45, Q46, Q47, Q48, Q49, Q50, Q51, Q52, Q53, Q54, Q55, Q56, Q57, Q58, Q59, Q60, Q61, Q62]), "operationType" : NewBodyOperationType.REMOVE, "oppositeDirection" : true, "depth" : 4 * mm, "offsetDistance" : 25 * mm});
        }
    });
